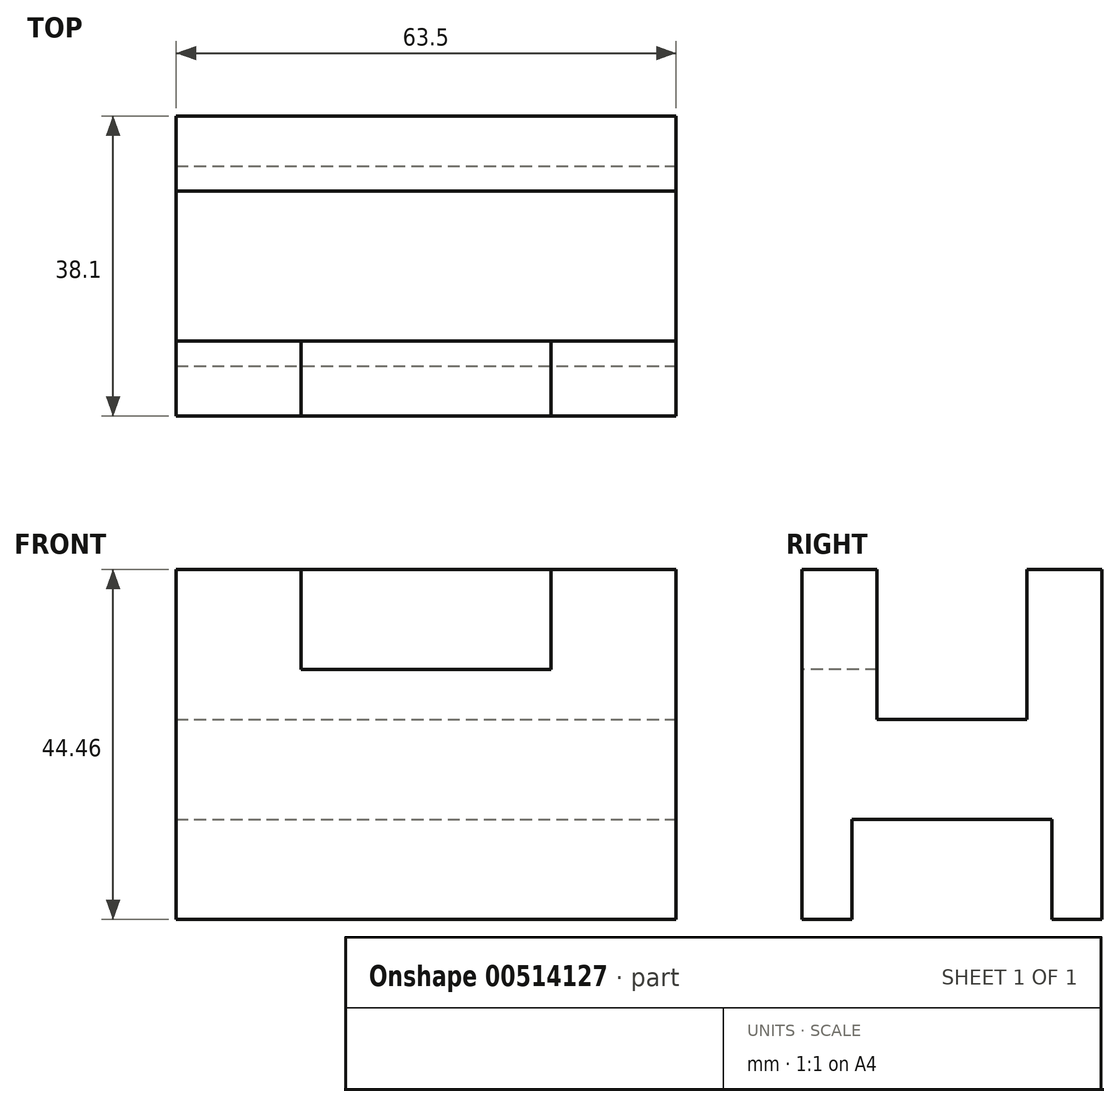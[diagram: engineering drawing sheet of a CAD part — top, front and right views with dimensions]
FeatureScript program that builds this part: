
annotation { "Feature Type Name" : "Feature", "Feature Type Description" : "" }
export const myFeature = defineFeature(function(context is Context, id is Id, definition is map)
    precondition{}
    {
        {
            var Q0;
            Q0=qCreatedBy(makeId("Front.planeOp"),FACE);
            var sketch = newSketch(context, id + "F0", { "sketchPlane" : qUnion([Q0])});
            skLineSegment(sketch, "E0.bottom", {"start": v(31.75, 22.23) * mm, "end": v(-31.75, 22.23) * mm});
            skLineSegment(sketch, "E0.top", {"start": v(31.75, -22.23) * mm, "end": v(-31.75, -22.23) * mm});
            skLineSegment(sketch, "E0.left", {"start": v(31.75, 22.22) * mm, "end": v(31.75, -22.23) * mm});
            skLineSegment(sketch, "E0.right", {"start": v(-31.75, 22.23) * mm, "end": v(-31.75, -22.23) * mm});
            skPoint(sketch, "E0.middle", {"position": v(0, 0) * mm});
            skSolve(sketch);
        }
        {
            var Q0;
            Q0=makeQuery(id+"F0.imprint","IMPRINT",FACE,{"disambiguationData":[TD([[makeQuery(id+"F0.imprint","IMPRINT",EDGE,{"derivedFrom":sQuery(id+"F0.wireOp",EDGE,"E0.bottom")}),1.0]])]});
            extrude(context, id + "F1", {"entities" : qUnion([Q0]), "depth" : 38.1 * mm});
        }
        {
            var Q0;
            Q0=makeQuery(id+"F1.opExtrude","SWEPT_FACE",FACE,{"disambiguationData":[OSD([sQuery(id+"F0.wireOp",EDGE,"E0.left")])]});
            var sketch = newSketch(context, id + "F2", { "sketchPlane" : qUnion([Q0])});
            skLineSegment(sketch, "E1.bottom", {"start": v(-28.57, 22.23) * mm, "end": v(-9.53, 22.23) * mm});
            skLineSegment(sketch, "E1.top", {"start": v(-28.57, 3.18) * mm, "end": v(-9.53, 3.18) * mm});
            skLineSegment(sketch, "E1.left", {"start": v(-28.58, 22.23) * mm, "end": v(-28.58, 3.18) * mm});
            skLineSegment(sketch, "E1.right", {"start": v(-9.53, 22.23) * mm, "end": v(-9.53, 3.18) * mm});
            skSolve(sketch);
        }
        {
            var Q0;
            Q0=makeQuery(id+"F2.imprint","IMPRINT",FACE,{"disambiguationData":[TD([[makeQuery(id+"F2.imprint","IMPRINT",EDGE,{"derivedFrom":sQuery(id+"F2.wireOp",EDGE,"E1.bottom")}),-1.0]])]});
            extrude(context, id + "F3", {"entities" : qUnion([Q0]), "operationType" : NewBodyOperationType.REMOVE, "oppositeDirection" : true, "depth" : 63.5 * mm});
        }
        {
            var Q0;
            Q0=makeQuery(id+"F1.opExtrude","SWEPT_FACE",FACE,{"disambiguationData":[OSD([sQuery(id+"F0.wireOp",EDGE,"E0.left")])]});
            var sketch = newSketch(context, id + "F4", { "sketchPlane" : qUnion([Q0])});
            skLineSegment(sketch, "E2.bottom", {"start": v(-31.75, -22.23) * mm, "end": v(-6.35, -22.23) * mm});
            skLineSegment(sketch, "E2.top", {"start": v(-31.75, -9.52) * mm, "end": v(-6.35, -9.52) * mm});
            skLineSegment(sketch, "E2.left", {"start": v(-31.75, -22.23) * mm, "end": v(-31.75, -9.53) * mm});
            skLineSegment(sketch, "E2.right", {"start": v(-6.35, -22.22) * mm, "end": v(-6.35, -9.52) * mm});
            skSolve(sketch);
        }
        {
            var Q0;
            Q0=makeQuery(id+"F4.imprint","IMPRINT",FACE,{"disambiguationData":[TD([[makeQuery(id+"F4.imprint","IMPRINT",EDGE,{"derivedFrom":sQuery(id+"F4.wireOp",EDGE,"E2.bottom")}),1.0]])]});
            extrude(context, id + "F5", {"entities" : qUnion([Q0]), "operationType" : NewBodyOperationType.REMOVE, "oppositeDirection" : true, "depth" : 63.5 * mm});
        }
        {
            var Q0;
            Q0=makeQuery(id+"F1.opExtrude","CAP_FACE",FACE,{"disambiguationData":[OSD([sQuery(id+"F0.wireOp",EDGE,"E0.bottom"),sQuery(id+"F0.wireOp",EDGE,"E0.top"),sQuery(id+"F0.wireOp",EDGE,"E0.left"),sQuery(id+"F0.wireOp",EDGE,"E0.right")])],"isStart":false});
            var sketch = newSketch(context, id + "F6", { "sketchPlane" : qUnion([Q0])});
            skLineSegment(sketch, "E3.bottom", {"start": v(-15.88, 22.23) * mm, "end": v(15.88, 22.23) * mm});
            skLineSegment(sketch, "E3.top", {"start": v(-15.88, 9.52) * mm, "end": v(15.88, 9.52) * mm});
            skLineSegment(sketch, "E3.left", {"start": v(-15.88, 22.23) * mm, "end": v(-15.88, 9.53) * mm});
            skLineSegment(sketch, "E3.right", {"start": v(15.88, 22.23) * mm, "end": v(15.88, 9.53) * mm});
            skSolve(sketch);
        }
        {
            var Q0;
            Q0=makeQuery(id+"F6.imprint","IMPRINT",FACE,{"disambiguationData":[TD([[makeQuery(id+"F6.imprint","IMPRINT",EDGE,{"derivedFrom":sQuery(id+"F6.wireOp",EDGE,"E3.bottom")}),1.0]])]});
            extrude(context, id + "F7", {"entities" : qUnion([Q0]), "operationType" : NewBodyOperationType.REMOVE, "oppositeDirection" : true, "depth" : 19.05 * mm});
        }
    });
